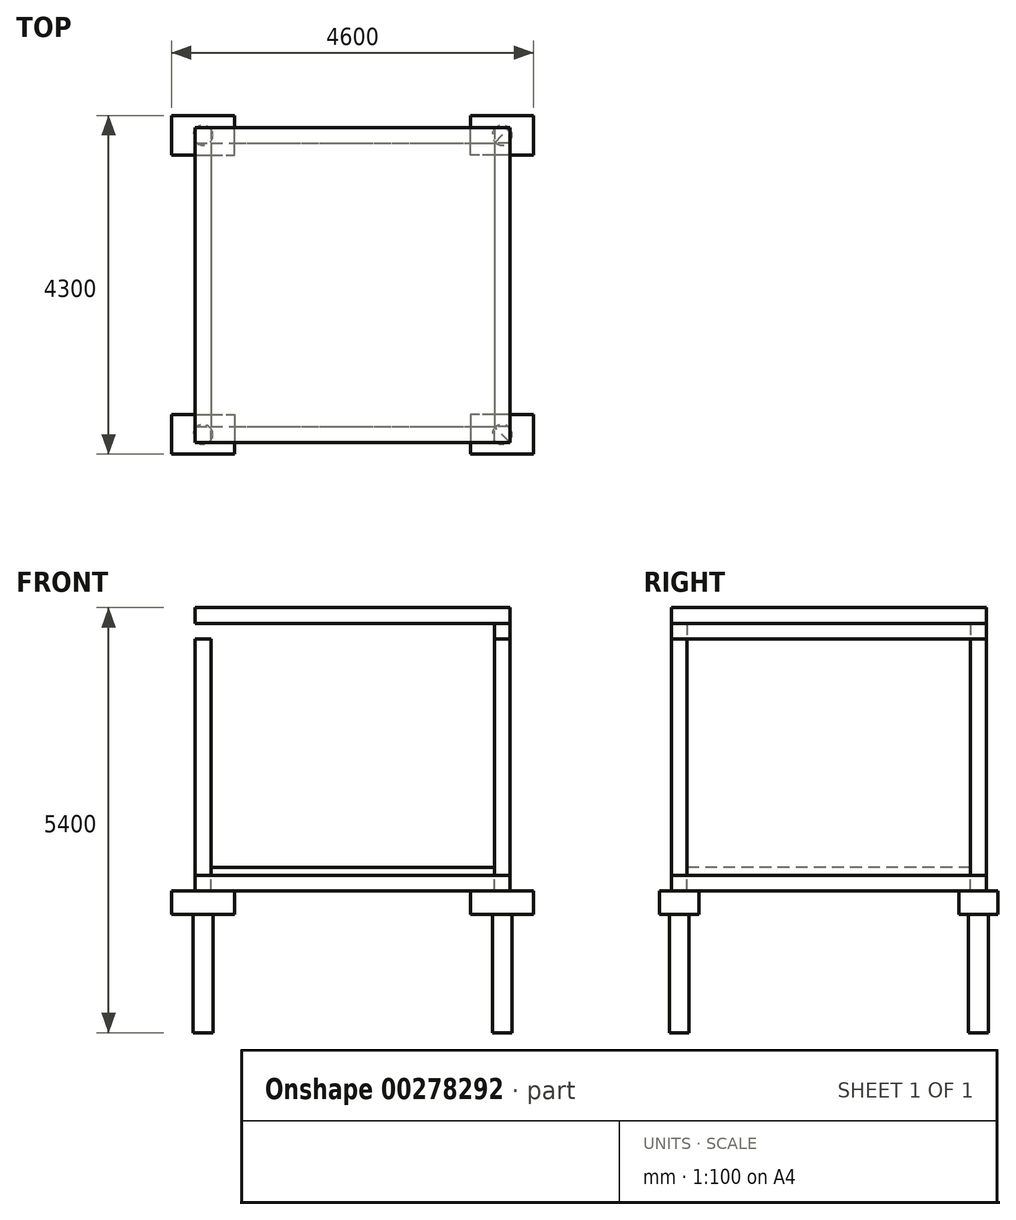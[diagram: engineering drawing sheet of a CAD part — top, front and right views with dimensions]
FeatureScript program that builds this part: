
annotation { "Feature Type Name" : "Feature", "Feature Type Description" : "" }
export const myFeature = defineFeature(function(context is Context, id is Id, definition is map)
    precondition{}
    {
        {
            var Q0;
            Q0=qCreatedBy(makeId("Top.planeOp"),FACE);
            var sketch = newSketch(context, id + "F0", { "sketchPlane" : qUnion([Q0])});
            skLineSegment(sketch, "E0.bottom", {"start": v(2000, 2000) * mm, "end": v(-2000, 2000) * mm, "construction": true});
            skLineSegment(sketch, "E0.top", {"start": v(2000, -2000) * mm, "end": v(-2000, -2000) * mm, "construction": true});
            skLineSegment(sketch, "E0.left", {"start": v(2000, 2000) * mm, "end": v(2000, -2000) * mm, "construction": true});
            skLineSegment(sketch, "E0.right", {"start": v(-2000, 2000) * mm, "end": v(-2000, -2000) * mm, "construction": true});
            skPoint(sketch, "E0.middle", {"position": v(0, 0) * mm});
            skLineSegment(sketch, "E1.bottom", {"start": v(-2000, -2000) * mm, "end": v(-1800, -2000) * mm});
            skLineSegment(sketch, "E1.top", {"start": v(-2000, -1800) * mm, "end": v(-1800, -1800) * mm});
            skLineSegment(sketch, "E1.left", {"start": v(-2000, -2000) * mm, "end": v(-2000, -1800) * mm});
            skLineSegment(sketch, "E1.right", {"start": v(-1800, -2000) * mm, "end": v(-1800, -1800) * mm});
            skLineSegment(sketch, "E2.bottom", {"start": v(2000, 2000) * mm, "end": v(1800, 2000) * mm});
            skLineSegment(sketch, "E2.top", {"start": v(2000, 1800) * mm, "end": v(1800, 1800) * mm});
            skLineSegment(sketch, "E2.left", {"start": v(2000, 2000) * mm, "end": v(2000, 1800) * mm});
            skLineSegment(sketch, "E2.right", {"start": v(1800, 2000) * mm, "end": v(1800, 1800) * mm});
            skLineSegment(sketch, "E3.bottom", {"start": v(-2000, 2000) * mm, "end": v(-1800, 2000) * mm});
            skLineSegment(sketch, "E3.top", {"start": v(-2000, 1800) * mm, "end": v(-1800, 1800) * mm});
            skLineSegment(sketch, "E3.left", {"start": v(-2000, 2000) * mm, "end": v(-2000, 1800) * mm});
            skLineSegment(sketch, "E3.right", {"start": v(-1800, 2000) * mm, "end": v(-1800, 1800) * mm});
            skLineSegment(sketch, "E4.bottom", {"start": v(2000, -2000) * mm, "end": v(1800, -2000) * mm});
            skLineSegment(sketch, "E4.top", {"start": v(2000, -1800) * mm, "end": v(1800, -1800) * mm});
            skLineSegment(sketch, "E4.left", {"start": v(2000, -2000) * mm, "end": v(2000, -1800) * mm});
            skLineSegment(sketch, "E4.right", {"start": v(1800, -2000) * mm, "end": v(1800, -1800) * mm});
            skSolve(sketch);
        }
        {
            var Q0;
            Q0 = qSketchRegion(id + "F0", true);
            extrude(context, id + "F1", {"entities" : qUnion([Q0]), "depth" : 3000 * mm});
        }
        {
            var Q0;
            Q0=qCreatedBy(makeId("Top.planeOp"),FACE);
            var sketch = newSketch(context, id + "F7", { "sketchPlane" : qUnion([Q0])});
            skLineSegment(sketch, "E5.0", {"start": v(2000, -2000) * mm, "end": v(-2000, -2000) * mm});
            skLineSegment(sketch, "E6.0", {"start": v(2000, 2000) * mm, "end": v(2000, -2000) * mm});
            skLineSegment(sketch, "E7.0", {"start": v(2000, 2000) * mm, "end": v(-2000, 2000) * mm});
            skLineSegment(sketch, "E8.0", {"start": v(-2000, 2000) * mm, "end": v(-2000, -2000) * mm});
            skPoint(sketch, "E9.0", {"position": v(-1800, 1800) * mm});
            skPoint(sketch, "E10.0", {"position": v(1800, -1800) * mm});
            skLineSegment(sketch, "E11.bottom", {"start": v(-1800, 1800) * mm, "end": v(1800, 1800) * mm});
            skLineSegment(sketch, "E11.top", {"start": v(-1800, -1800) * mm, "end": v(1800, -1800) * mm});
            skLineSegment(sketch, "E11.left", {"start": v(-1800, 1800) * mm, "end": v(-1800, -1800) * mm});
            skLineSegment(sketch, "E11.right", {"start": v(1800, 1800) * mm, "end": v(1800, -1800) * mm});
            skSolve(sketch);
        }
        {
            var Q0;
            Q0=makeQuery(id+"F7.imprint","IMPRINT",FACE,{"disambiguationData":[TD([[makeQuery(id+"F7.imprint","IMPRINT",EDGE,{"derivedFrom":sQuery(id+"F7.wireOp",EDGE,"E5.0")}),-1.0]])]});
            extrude(context, id + "F8", {"entities" : qUnion([Q0]), "oppositeDirection" : true, "depth" : 200 * mm});
        }
        {
            var Q0;
            Q0=makeQuery(id+"F8.opExtrude","CAP_FACE",FACE,{"disambiguationData":[OSD([sQuery(id+"F7.wireOp",EDGE,"E5.0"),sQuery(id+"F7.wireOp",EDGE,"E6.0"),sQuery(id+"F7.wireOp",EDGE,"E7.0"),sQuery(id+"F7.wireOp",EDGE,"E8.0"),sQuery(id+"F7.wireOp",EDGE,"E11.bottom"),sQuery(id+"F7.wireOp",EDGE,"E11.top"),sQuery(id+"F7.wireOp",EDGE,"E11.left"),sQuery(id+"F7.wireOp",EDGE,"E11.right")])],"isStart":false});
            var sketch = newSketch(context, id + "F2", { "sketchPlane" : qUnion([Q0])});
            skPoint(sketch, "E12.0", {"position": v(1800, 1800) * mm});
            skPoint(sketch, "E13.0", {"position": v(2000, 2000) * mm});
            skPoint(sketch, "E14.0", {"position": v(-2000, 2000) * mm});
            skPoint(sketch, "E15.0", {"position": v(-1800, 1800) * mm});
            skPoint(sketch, "E16.0", {"position": v(-2000, -2000) * mm});
            skPoint(sketch, "E17.0", {"position": v(-1800, -1800) * mm});
            skPoint(sketch, "E18.0", {"position": v(2000, -2000) * mm});
            skPoint(sketch, "E19.0", {"position": v(1800, -1800) * mm});
            skLineSegment(sketch, "E20", {"start": v(1800, -1800) * mm, "end": v(2000, -2000) * mm, "construction": true});
            skLineSegment(sketch, "E21", {"start": v(2000, 2000) * mm, "end": v(1800, 1800) * mm, "construction": true});
            skLineSegment(sketch, "E22", {"start": v(-1800, -1800) * mm, "end": v(-2000, -2000) * mm, "construction": true});
            skLineSegment(sketch, "E23.bottom", {"start": v(-2300, -1650) * mm, "end": v(-1500, -1650) * mm});
            skLineSegment(sketch, "E23.top", {"start": v(-2300, -2150) * mm, "end": v(-1500, -2150) * mm});
            skLineSegment(sketch, "E23.left", {"start": v(-2300, -1650) * mm, "end": v(-2300, -2150) * mm});
            skLineSegment(sketch, "E23.right", {"start": v(-1500, -1650) * mm, "end": v(-1500, -2150) * mm});
            skPoint(sketch, "E23.middle", {"position": v(-1900, -1900) * mm});
            skLineSegment(sketch, "E24", {"start": v(-1800, 1800) * mm, "end": v(-2000, 2000) * mm, "construction": true});
            skLineSegment(sketch, "E25.bottom", {"start": v(-2300, 1650) * mm, "end": v(-1500, 1650) * mm});
            skLineSegment(sketch, "E25.top", {"start": v(-2300, 2150) * mm, "end": v(-1500, 2150) * mm});
            skLineSegment(sketch, "E25.left", {"start": v(-2300, 1650) * mm, "end": v(-2300, 2150) * mm});
            skLineSegment(sketch, "E25.right", {"start": v(-1500, 1650) * mm, "end": v(-1500, 2150) * mm});
            skPoint(sketch, "E25.middle", {"position": v(-1900, 1900) * mm});
            skLineSegment(sketch, "E26.bottom", {"start": v(2300, -1650) * mm, "end": v(1500, -1650) * mm});
            skLineSegment(sketch, "E26.top", {"start": v(2300, -2150) * mm, "end": v(1500, -2150) * mm});
            skLineSegment(sketch, "E26.left", {"start": v(2300, -1650) * mm, "end": v(2300, -2150) * mm});
            skLineSegment(sketch, "E26.right", {"start": v(1500, -1650) * mm, "end": v(1500, -2150) * mm});
            skPoint(sketch, "E26.middle", {"position": v(1900, -1900) * mm});
            skLineSegment(sketch, "E27.bottom", {"start": v(2300, 1650) * mm, "end": v(1500, 1650) * mm});
            skLineSegment(sketch, "E27.top", {"start": v(2300, 2150) * mm, "end": v(1500, 2150) * mm});
            skLineSegment(sketch, "E27.left", {"start": v(2300, 1650) * mm, "end": v(2300, 2150) * mm});
            skLineSegment(sketch, "E27.right", {"start": v(1500, 1650) * mm, "end": v(1500, 2150) * mm});
            skPoint(sketch, "E27.middle", {"position": v(1900, 1900) * mm});
            skSolve(sketch);
        }
        {
            var Q0;
            Q0 = qSketchRegion(id + "F2", true);
            extrude(context, id + "F9", {"entities" : qUnion([Q0]), "operationType" : NewBodyOperationType.ADD, "depth" : 300 * mm});
        }
        {
            var Q0;
            Q0=makeQuery(id+"F9.opExtrude","CAP_FACE",FACE,{"disambiguationData":[OSD([sQuery(id+"F2.wireOp",EDGE,"E27.bottom"),sQuery(id+"F2.wireOp",EDGE,"E27.top"),sQuery(id+"F2.wireOp",EDGE,"E27.left"),sQuery(id+"F2.wireOp",EDGE,"E27.right")])],"isStart":false});
            var sketch = newSketch(context, id + "F3", { "sketchPlane" : qUnion([Q0])});
            skPoint(sketch, "E28.0", {"position": v(2300, 2150) * mm});
            skPoint(sketch, "E29.0", {"position": v(1500, 1650) * mm});
            skPoint(sketch, "E30.0", {"position": v(-2300, -2150) * mm});
            skPoint(sketch, "E31.0", {"position": v(-1500, -1650) * mm});
            skPoint(sketch, "E32.0", {"position": v(-2300, 2150) * mm});
            skPoint(sketch, "E33.0", {"position": v(-1500, 1650) * mm});
            skPoint(sketch, "E34.0", {"position": v(1500, -1650) * mm});
            skPoint(sketch, "E35.0", {"position": v(2300, -2150) * mm});
            skLineSegment(sketch, "E36", {"start": v(1500, -1650) * mm, "end": v(2300, -2150) * mm, "construction": true});
            skLineSegment(sketch, "E37", {"start": v(-2300, 2150) * mm, "end": v(-1500, 1650) * mm, "construction": true});
            skLineSegment(sketch, "E38", {"start": v(-2300, -2150) * mm, "end": v(-1500, -1650) * mm, "construction": true});
            skLineSegment(sketch, "E39", {"start": v(1500, 1650) * mm, "end": v(2300, 2150) * mm, "construction": true});
            skCircle(sketch, "E40", {"center": v(1900, 1900) * mm, "radius": 125 * mm});
            skCircle(sketch, "E41", {"center": v(-1900, 1900) * mm, "radius": 125 * mm});
            skCircle(sketch, "E42", {"center": v(-1900, -1900) * mm, "radius": 125 * mm});
            skCircle(sketch, "E43", {"center": v(1900, -1900) * mm, "radius": 125 * mm});
            skSolve(sketch);
        }
        {
            var Q0;
            Q0 = qSketchRegion(id + "F3", true);
            extrude(context, id + "F10", {"entities" : qUnion([Q0]), "operationType" : NewBodyOperationType.ADD, "depth" : 1500 * mm});
        }
        {
            var Q0;
            Q0=qCreatedBy(makeId("Top.planeOp"),FACE);
            var sketch = newSketch(context, id + "F11", { "sketchPlane" : qUnion([Q0])});
            skPoint(sketch, "E44.0", {"position": v(1800, -1800) * mm});
            skPoint(sketch, "E45.0", {"position": v(-1800, 1800) * mm});
            skLineSegment(sketch, "E46.bottom", {"start": v(-1800, 1800) * mm, "end": v(1800, 1800) * mm});
            skLineSegment(sketch, "E46.top", {"start": v(-1800, -1800) * mm, "end": v(1800, -1800) * mm});
            skLineSegment(sketch, "E46.left", {"start": v(-1800, 1800) * mm, "end": v(-1800, -1800) * mm});
            skLineSegment(sketch, "E46.right", {"start": v(1800, 1800) * mm, "end": v(1800, -1800) * mm});
            skSolve(sketch);
        }
        {
            var Q0;
            Q0 = qSketchRegion(id + "F11", true);
            extrude(context, id + "F12", {"entities" : qUnion([Q0]), "depth" : 100 * mm});
        }
        {
            var Q0;
            Q0=makeQuery(id+"F1.opExtrude","CAP_FACE",FACE,{"disambiguationData":[OSD([sQuery(id+"F0.wireOp",EDGE,"E4.bottom"),sQuery(id+"F0.wireOp",EDGE,"E4.top"),sQuery(id+"F0.wireOp",EDGE,"E4.left"),sQuery(id+"F0.wireOp",EDGE,"E4.right")])],"isStart":false});
            var sketch = newSketch(context, id + "F4", { "sketchPlane" : qUnion([Q0])});
            skPoint(sketch, "E47.0", {"position": v(2000, -2000) * mm});
            skPoint(sketch, "E48.0", {"position": v(1800, -1800) * mm});
            skPoint(sketch, "E49.0", {"position": v(1800, 1800) * mm});
            skPoint(sketch, "E50.0", {"position": v(2000, 2000) * mm});
            skLineSegment(sketch, "E51", {"start": v(1800, -1800) * mm, "end": v(1800, 1800) * mm});
            skLineSegment(sketch, "E52", {"start": v(2000, -2000) * mm, "end": v(2000, 2000) * mm});
            skLineSegment(sketch, "E53", {"start": v(1800, 1800) * mm, "end": v(2000, 2000) * mm});
            skLineSegment(sketch, "E54", {"start": v(2000, -2000) * mm, "end": v(1800, -1800) * mm});
            skSolve(sketch);
        }
        {
            var Q0;
            Q0 = qSketchRegion(id + "F4", true);
            extrude(context, id + "F5", {"entities" : qUnion([Q0]), "depth" : 200 * mm});
        }
        {
            var Q0;
            Q0=makeQuery(id+"F8.opExtrude","CAP_FACE",FACE,{"disambiguationData":[OSD([sQuery(id+"F7.wireOp",EDGE,"E5.0"),sQuery(id+"F7.wireOp",EDGE,"E6.0"),sQuery(id+"F7.wireOp",EDGE,"E7.0"),sQuery(id+"F7.wireOp",EDGE,"E8.0"),sQuery(id+"F7.wireOp",EDGE,"E11.bottom"),sQuery(id+"F7.wireOp",EDGE,"E11.top"),sQuery(id+"F7.wireOp",EDGE,"E11.left"),sQuery(id+"F7.wireOp",EDGE,"E11.right")])],"isStart":true});
            var sketch = newSketch(context, id + "F13", { "sketchPlane" : qUnion([Q0])});
            skPoint(sketch, "E55.0", {"position": v(2000, -1800) * mm});
            skPoint(sketch, "E56", {"position": v(1800, 1800) * mm});
            skLineSegment(sketch, "E57.bottom", {"start": v(2000, -1800) * mm, "end": v(1800, -1800) * mm});
            skLineSegment(sketch, "E57.top", {"start": v(2000, 1800) * mm, "end": v(1800, 1800) * mm});
            skLineSegment(sketch, "E57.left", {"start": v(2000, -1800) * mm, "end": v(2000, 1800) * mm});
            skLineSegment(sketch, "E57.right", {"start": v(1800, -1800) * mm, "end": v(1800, 1800) * mm});
            skSolve(sketch);
        }
        {
            var Q0;
            Q0 = qSketchRegion(id + "F13", true);
            extrude(context, id + "F6", {"entities" : qUnion([Q0]), "depth" : 3000 * mm});
        }
        {
            var Q0;
            Q0=makeQuery(id+"F5.opExtrude","CAP_FACE",FACE,{"disambiguationData":[OSD([sQuery(id+"F4.wireOp",EDGE,"E51"),sQuery(id+"F4.wireOp",EDGE,"E52"),sQuery(id+"F4.wireOp",EDGE,"E53"),sQuery(id+"F4.wireOp",EDGE,"E54")])],"isStart":false});
            var sketch = newSketch(context, id + "F14", { "sketchPlane" : qUnion([Q0])});
            skPoint(sketch, "E58.0", {"position": v(2000, -2000) * mm});
            skPoint(sketch, "E59.0", {"position": v(2000, 2000) * mm});
            skLineSegment(sketch, "E60.bottom", {"start": v(2000, -2000) * mm, "end": v(-2000, -2000) * mm});
            skLineSegment(sketch, "E60.top", {"start": v(2000, 2000) * mm, "end": v(-2000, 2000) * mm});
            skLineSegment(sketch, "E60.left", {"start": v(2000, -2000) * mm, "end": v(2000, 2000) * mm});
            skLineSegment(sketch, "E60.right", {"start": v(-2000, -2000) * mm, "end": v(-2000, 2000) * mm});
            skSolve(sketch);
        }
        {
            var Q0;
            Q0 = qSketchRegion(id + "F14", true);
            extrude(context, id + "F15", {"entities" : qUnion([Q0]), "depth" : 200 * mm});
        }
    });
